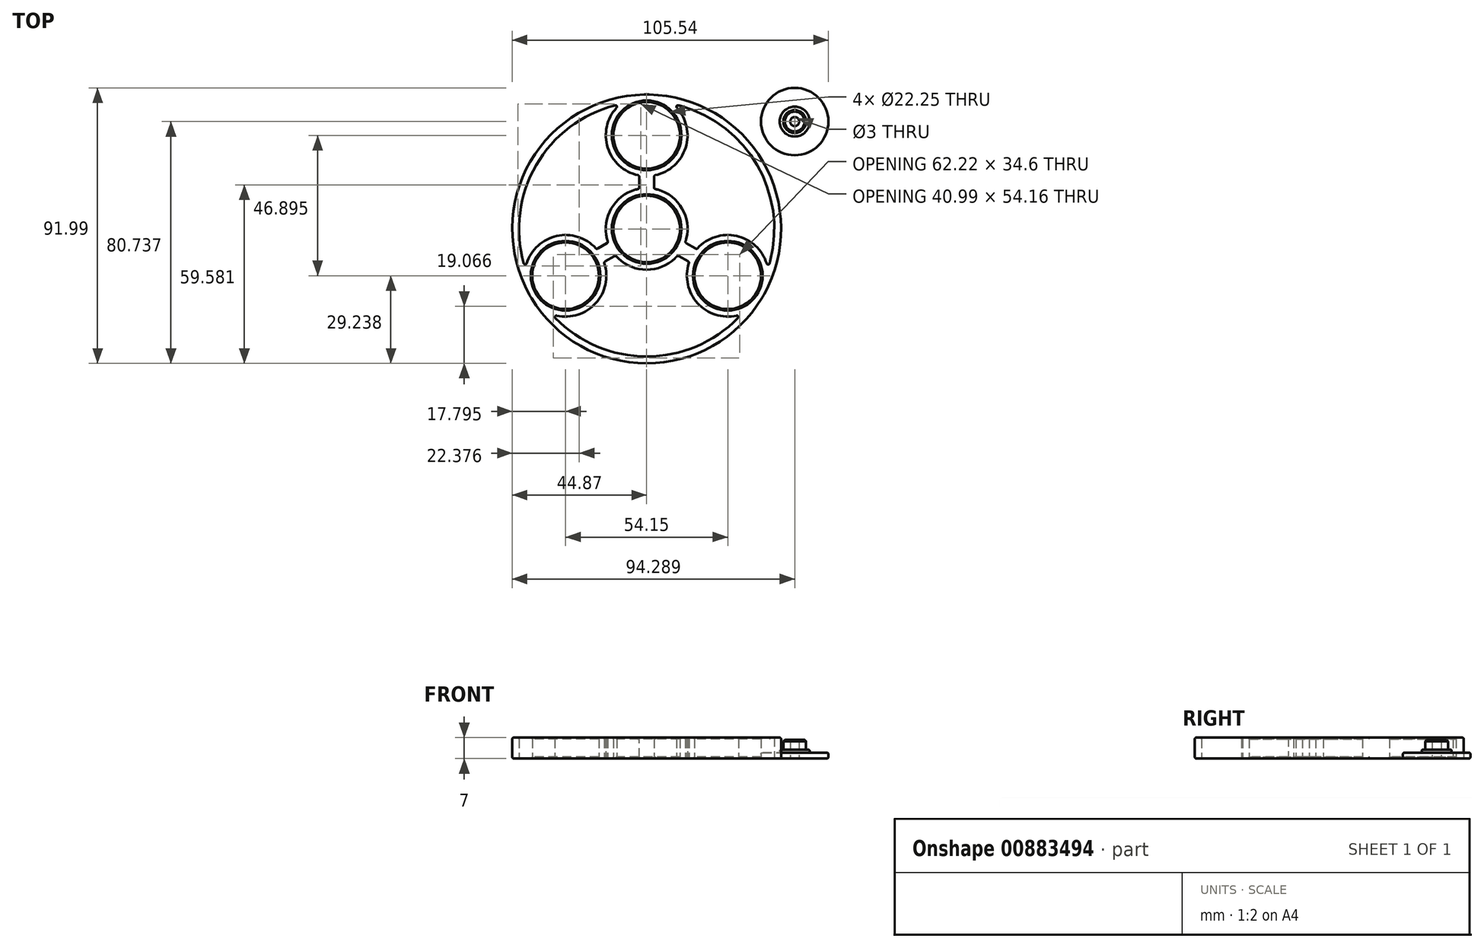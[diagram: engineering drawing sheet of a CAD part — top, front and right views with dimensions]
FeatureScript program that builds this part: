
annotation { "Feature Type Name" : "Feature", "Feature Type Description" : "" }
export const myFeature = defineFeature(function(context is Context, id is Id, definition is map)
    precondition{}
    {
        {
            var Q0;
            Q0=qCreatedBy(makeId("Top.planeOp"),FACE);
            var sketch = newSketch(context, id + "F0", { "sketchPlane" : qUnion([Q0])});
            skCircle(sketch, "E0", {"center": v(0, 0) * mm, "radius": 11.12 * mm});
            skArc(sketch, "E1", {"start": v(-2.5, 13.4) * mm, "mid": v(-11.8, 6.81) * mm, "end": v(-12.85, -4.53) * mm});
            skCircle(sketch, "E2", {"center": v(0, 31.26) * mm, "radius": 11.12 * mm});
            skArc(sketch, "E3", {"start": v(2.5, 17.87) * mm, "mid": v(13.18, 27.8) * mm, "end": v(8.76, 41.7) * mm});
            skLineSegment(sketch, "E4", {"start": v(-2.5, 17.87) * mm, "end": v(-2.5, 13.4) * mm});
            skLineSegment(sketch, "E5", {"start": v(2.5, 17.87) * mm, "end": v(2.5, 13.4) * mm});
            skArc(sketch, "E6.1.0", {"start": v(-16.73, -6.77) * mm, "mid": v(-30.66, -2.49) * mm, "end": v(-40.5, -13.26) * mm});
            skCircle(sketch, "E6.1.1", {"center": v(-27.07, -15.63) * mm, "radius": 11.12 * mm});
            skArc(sketch, "E6.1.2", {"start": v(-10.35, -8.86) * mm, "mid": v(0, -13.63) * mm, "end": v(10.35, -8.86) * mm});
            skLineSegment(sketch, "E6.1.4", {"start": v(-14.23, -11.1) * mm, "end": v(-10.35, -8.86) * mm});
            skLineSegment(sketch, "E6.1.5", {"start": v(-16.73, -6.77) * mm, "end": v(-12.85, -4.53) * mm});
            skArc(sketch, "E6.2.0", {"start": v(14.23, -11.1) * mm, "mid": v(17.49, -25.31) * mm, "end": v(31.73, -28.44) * mm});
            skCircle(sketch, "E6.2.1", {"center": v(27.07, -15.63) * mm, "radius": 11.12 * mm});
            skArc(sketch, "E6.2.2", {"start": v(12.85, -4.53) * mm, "mid": v(11.8, 6.81) * mm, "end": v(2.5, 13.4) * mm});
            skLineSegment(sketch, "E6.2.4", {"start": v(16.73, -6.77) * mm, "end": v(12.85, -4.53) * mm});
            skLineSegment(sketch, "E6.2.5", {"start": v(14.23, -11.1) * mm, "end": v(10.35, -8.86) * mm});
            skArc(sketch, "E7.trimOffspring", {"start": v(-10.35, -8.86) * mm, "mid": v(0, -13.62) * mm, "end": v(10.35, -8.86) * mm});
            skCircle(sketch, "E8", {"center": v(0, 0) * mm, "radius": 44.87 * mm});
            skArc(sketch, "E9", {"start": v(-31.73, -28.44) * mm, "mid": v(0, -42.6) * mm, "end": v(31.73, -28.44) * mm});
            skArc(sketch, "E10.trimOffspring", {"start": v(-39.26, -21.72) * mm, "mid": v(-38.87, -22.44) * mm, "end": v(-38.44, -23.14) * mm});
            skArc(sketch, "E11.trimOffspring", {"start": v(-31.73, -28.44) * mm, "mid": v(-17.49, -25.31) * mm, "end": v(-14.23, -11.1) * mm});
            skArc(sketch, "E12.trimOffspring", {"start": v(-8.76, 41.7) * mm, "mid": v(-36.9, 21.3) * mm, "end": v(-40.5, -13.26) * mm});
            skArc(sketch, "E13.trimOffspring", {"start": v(-8.76, 41.7) * mm, "mid": v(-13.18, 27.8) * mm, "end": v(-2.5, 17.87) * mm});
            skArc(sketch, "E14.trimOffspring", {"start": v(0.82, 44.86) * mm, "mid": v(0, 44.89) * mm, "end": v(-0.82, 44.86) * mm});
            skArc(sketch, "E15.trimOffspring", {"start": v(40.5, -13.26) * mm, "mid": v(30.66, -2.49) * mm, "end": v(16.73, -6.77) * mm});
            skArc(sketch, "E16.trimOffspring", {"start": v(40.5, -13.26) * mm, "mid": v(36.9, 21.3) * mm, "end": v(8.76, 41.7) * mm});
            skArc(sketch, "E17.trimOffspring", {"start": v(38.44, -23.14) * mm, "mid": v(38.87, -22.44) * mm, "end": v(39.26, -21.72) * mm});
            skSolve(sketch);
        }
        {
            var Q0;
            Q0 = qSketchRegion(id + "F0", true);
            extrude(context, id + "F1", {"entities" : qUnion([Q0]), "depth" : 7 * mm, "offsetDistance" : 25 * mm});
        }
        {
            var Q0;
            Q0=makeQuery(id+"F1.opExtrude","CAP_EDGE",EDGE,{"disambiguationData":[OSD([sQuery(id+"F0.wireOp",EDGE,"E6.2.0")])],"isStart":false});
            var Q1;
            Q1=makeQuery(id+"F1.opExtrude","CAP_EDGE",EDGE,{"disambiguationData":[OSD([sQuery(id+"F0.wireOp",EDGE,"E6.2.2")])],"isStart":false});
            var Q2;
            {var subQ0=sQuery(id+"F0.wireOp",EDGE,"E8");Q2=makeQuery(id+"F1.opExtrude","CAP_EDGE",EDGE,{"disambiguationData":[OSD([subQ0]),TDD([makeQuery(id+"F0.imprint","IMPRINT",EDGE,{"disambiguationData":[TD([[makeQuery(id+"F0.imprint","INTERSECT",VERTEX,{"disambiguationData":[OD(0.0)],"derivedFrom":[subQ0,sQuery(id+"F0.wireOp",EDGE,"E14.trimOffspring")]}),1.0]])],"derivedFrom":subQ0})])],"isStart":false});}
            var Q3;
            {var subQ0=sQuery(id+"F0.wireOp",EDGE,"E8");Q3=makeQuery(id+"F1.opExtrude","CAP_EDGE",EDGE,{"disambiguationData":[OSD([subQ0]),TDD([makeQuery(id+"F0.imprint","IMPRINT",EDGE,{"disambiguationData":[TD([[makeQuery(id+"F0.imprint","INTERSECT",VERTEX,{"disambiguationData":[OD(1.0)],"derivedFrom":[subQ0,sQuery(id+"F0.wireOp",EDGE,"E10.trimOffspring")]}),-1.0]])],"derivedFrom":subQ0})])],"isStart":false});}
            var Q4;
            Q4=makeQuery(id+"F1.opExtrude","CAP_EDGE",EDGE,{"disambiguationData":[OSD([sQuery(id+"F0.wireOp",EDGE,"E7.trimOffspring")])],"isStart":false});
            var Q5;
            Q5=makeQuery(id+"F1.opExtrude","CAP_EDGE",EDGE,{"disambiguationData":[OSD([sQuery(id+"F0.wireOp",EDGE,"E1")])],"isStart":false});
            var Q6;
            Q6=makeQuery(id+"F1.opExtrude","CAP_EDGE",EDGE,{"disambiguationData":[OSD([sQuery(id+"F0.wireOp",EDGE,"E9")])],"isStart":false});
            var Q7;
            Q7=makeQuery(id+"F1.opExtrude","CAP_EDGE",EDGE,{"disambiguationData":[OSD([sQuery(id+"F0.wireOp",EDGE,"E4")])],"isStart":false});
            var Q8;
            Q8=makeQuery(id+"F1.opExtrude","CAP_EDGE",EDGE,{"disambiguationData":[OSD([sQuery(id+"F0.wireOp",EDGE,"E15.trimOffspring")])],"isStart":false});
            var Q9;
            Q9=makeQuery(id+"F1.opExtrude","CAP_EDGE",EDGE,{"disambiguationData":[OSD([sQuery(id+"F0.wireOp",EDGE,"E5")])],"isStart":false});
            var Q10;
            Q10=makeQuery(id+"F1.opExtrude","CAP_EDGE",EDGE,{"disambiguationData":[OSD([sQuery(id+"F0.wireOp",EDGE,"E13.trimOffspring")])],"isStart":false});
            var Q11;
            Q11=makeQuery(id+"F1.opExtrude","CAP_EDGE",EDGE,{"disambiguationData":[OSD([sQuery(id+"F0.wireOp",EDGE,"E6.1.0")])],"isStart":false});
            var Q12;
            {var subQ0=sQuery(id+"F0.wireOp",EDGE,"E8");Q12=makeQuery(id+"F1.opExtrude","CAP_EDGE",EDGE,{"disambiguationData":[OSD([subQ0]),TDD([makeQuery(id+"F0.imprint","IMPRINT",EDGE,{"disambiguationData":[TD([[makeQuery(id+"F0.imprint","INTERSECT",VERTEX,{"disambiguationData":[OD(0.0)],"derivedFrom":[subQ0,sQuery(id+"F0.wireOp",EDGE,"E10.trimOffspring")]}),1.0]])],"derivedFrom":subQ0})])],"isStart":false});}
            var Q13;
            Q13=makeQuery(id+"F1.opExtrude","CAP_EDGE",EDGE,{"disambiguationData":[OSD([sQuery(id+"F0.wireOp",EDGE,"E11.trimOffspring")])],"isStart":false});
            var Q14;
            Q14=makeQuery(id+"F1.opExtrude","CAP_EDGE",EDGE,{"disambiguationData":[OSD([sQuery(id+"F0.wireOp",EDGE,"E3")])],"isStart":false});
            var Q15;
            Q15=makeQuery(id+"F1.opExtrude","CAP_EDGE",EDGE,{"disambiguationData":[OSD([sQuery(id+"F0.wireOp",EDGE,"E12.trimOffspring")])],"isStart":false});
            var Q16;
            Q16=makeQuery(id+"F1.opExtrude","CAP_EDGE",EDGE,{"disambiguationData":[OSD([sQuery(id+"F0.wireOp",EDGE,"E6.1.0")])],"isStart":true});
            var Q17;
            Q17=makeQuery(id+"F1.opExtrude","SWEPT_EDGE",EDGE,{"disambiguationData":[OSD([sQuery(id+"F0.wireOp",EDGE,"E4"),sQuery(id+"F0.wireOp",EDGE,"E1")])]});
            var Q18;
            Q18=makeQuery(id+"F1.opExtrude","CAP_EDGE",EDGE,{"disambiguationData":[OSD([sQuery(id+"F0.wireOp",EDGE,"E11.trimOffspring")])],"isStart":true});
            var Q19;
            Q19=makeQuery(id+"F1.opExtrude","SWEPT_EDGE",EDGE,{"disambiguationData":[OSD([sQuery(id+"F0.wireOp",EDGE,"E6.1.4"),sQuery(id+"F0.wireOp",EDGE,"E7.trimOffspring")])]});
            var Q20;
            Q20=makeQuery(id+"F1.opExtrude","CAP_EDGE",EDGE,{"disambiguationData":[OSD([sQuery(id+"F0.wireOp",EDGE,"E6.2.4")])],"isStart":false});
            var Q21;
            Q21=makeQuery(id+"F1.opExtrude","SWEPT_EDGE",EDGE,{"disambiguationData":[OSD([sQuery(id+"F0.wireOp",EDGE,"E6.1.0"),sQuery(id+"F0.wireOp",EDGE,"E6.1.5")])]});
            var Q22;
            {var subQ0=sQuery(id+"F0.wireOp",EDGE,"E8");Q22=makeQuery(id+"F1.opExtrude","CAP_EDGE",EDGE,{"disambiguationData":[OSD([subQ0]),TDD([makeQuery(id+"F0.imprint","IMPRINT",EDGE,{"disambiguationData":[TD([[makeQuery(id+"F0.imprint","INTERSECT",VERTEX,{"disambiguationData":[OD(0.0)],"derivedFrom":[subQ0,sQuery(id+"F0.wireOp",EDGE,"E10.trimOffspring")]}),1.0]])],"derivedFrom":subQ0})])],"isStart":true});}
            var Q23;
            Q23=makeQuery(id+"F1.opExtrude","CAP_EDGE",EDGE,{"disambiguationData":[OSD([sQuery(id+"F0.wireOp",EDGE,"E15.trimOffspring")])],"isStart":true});
            var Q24;
            Q24=makeQuery(id+"F1.opExtrude","SWEPT_EDGE",EDGE,{"disambiguationData":[OSD([sQuery(id+"F0.wireOp",EDGE,"E3"),sQuery(id+"F0.wireOp",EDGE,"E5")])]});
            var Q25;
            Q25=makeQuery(id+"F1.opExtrude","SWEPT_EDGE",EDGE,{"disambiguationData":[OSD([sQuery(id+"F0.wireOp",EDGE,"E6.1.0"),sQuery(id+"F0.wireOp",EDGE,"E12.trimOffspring")])]});
            var Q26;
            Q26=makeQuery(id+"F1.opExtrude","CAP_EDGE",EDGE,{"disambiguationData":[OSD([sQuery(id+"F0.wireOp",EDGE,"E14.trimOffspring")])],"isStart":false});
            var Q27;
            Q27=makeQuery(id+"F1.opExtrude","SWEPT_EDGE",EDGE,{"disambiguationData":[OSD([sQuery(id+"F0.wireOp",EDGE,"E6.2.4"),sQuery(id+"F0.wireOp",EDGE,"E6.2.2")])]});
            var Q28;
            Q28=makeQuery(id+"F1.opExtrude","CAP_EDGE",EDGE,{"disambiguationData":[OSD([sQuery(id+"F0.wireOp",EDGE,"E9")])],"isStart":true});
            var Q29;
            Q29=makeQuery(id+"F1.opExtrude","CAP_EDGE",EDGE,{"disambiguationData":[OSD([sQuery(id+"F0.wireOp",EDGE,"E6.1.4")])],"isStart":false});
            var Q30;
            Q30=makeQuery(id+"F1.opExtrude","CAP_EDGE",EDGE,{"disambiguationData":[OSD([sQuery(id+"F0.wireOp",EDGE,"E3")])],"isStart":true});
            var Q31;
            Q31=makeQuery(id+"F1.opExtrude","SWEPT_EDGE",EDGE,{"disambiguationData":[OSD([sQuery(id+"F0.wireOp",EDGE,"E5"),sQuery(id+"F0.wireOp",EDGE,"E6.2.2")])]});
            var Q32;
            {var subQ0=sQuery(id+"F0.wireOp",EDGE,"E8");Q32=makeQuery(id+"F1.opExtrude","CAP_EDGE",EDGE,{"disambiguationData":[OSD([subQ0]),TDD([makeQuery(id+"F0.imprint","IMPRINT",EDGE,{"disambiguationData":[TD([[makeQuery(id+"F0.imprint","INTERSECT",VERTEX,{"disambiguationData":[OD(0.0)],"derivedFrom":[subQ0,sQuery(id+"F0.wireOp",EDGE,"E14.trimOffspring")]}),1.0]])],"derivedFrom":subQ0})])],"isStart":true});}
            var Q33;
            Q33=makeQuery(id+"F1.opExtrude","CAP_EDGE",EDGE,{"disambiguationData":[OSD([sQuery(id+"F0.wireOp",EDGE,"E6.2.5")])],"isStart":false});
            var Q34;
            Q34=makeQuery(id+"F1.opExtrude","CAP_EDGE",EDGE,{"disambiguationData":[OSD([sQuery(id+"F0.wireOp",EDGE,"E10.trimOffspring")])],"isStart":false});
            var Q35;
            Q35=makeQuery(id+"F1.opExtrude","CAP_EDGE",EDGE,{"disambiguationData":[OSD([sQuery(id+"F0.wireOp",EDGE,"E17.trimOffspring")])],"isStart":false});
            var Q36;
            Q36=makeQuery(id+"F1.opExtrude","CAP_EDGE",EDGE,{"disambiguationData":[OSD([sQuery(id+"F0.wireOp",EDGE,"E7.trimOffspring")])],"isStart":true});
            var Q37;
            Q37=makeQuery(id+"F1.opExtrude","CAP_EDGE",EDGE,{"disambiguationData":[OSD([sQuery(id+"F0.wireOp",EDGE,"E6.2.2")])],"isStart":true});
            var Q38;
            Q38=makeQuery(id+"F1.opExtrude","CAP_EDGE",EDGE,{"disambiguationData":[OSD([sQuery(id+"F0.wireOp",EDGE,"E12.trimOffspring")])],"isStart":true});
            var Q39;
            Q39=makeQuery(id+"F1.opExtrude","SWEPT_EDGE",EDGE,{"disambiguationData":[OSD([sQuery(id+"F0.wireOp",EDGE,"E6.2.4"),sQuery(id+"F0.wireOp",EDGE,"E15.trimOffspring")])]});
            var Q40;
            Q40=makeQuery(id+"F1.opExtrude","CAP_EDGE",EDGE,{"disambiguationData":[OSD([sQuery(id+"F0.wireOp",EDGE,"E13.trimOffspring")])],"isStart":true});
            var Q41;
            Q41=makeQuery(id+"F1.opExtrude","SWEPT_EDGE",EDGE,{"disambiguationData":[OSD([sQuery(id+"F0.wireOp",EDGE,"E15.trimOffspring"),sQuery(id+"F0.wireOp",EDGE,"E16.trimOffspring")])]});
            var Q42;
            Q42=makeQuery(id+"F1.opExtrude","SWEPT_EDGE",EDGE,{"disambiguationData":[OSD([sQuery(id+"F0.wireOp",EDGE,"E9"),sQuery(id+"F0.wireOp",EDGE,"E11.trimOffspring")])]});
            var Q43;
            {var subQ0=sQuery(id+"F0.wireOp",EDGE,"E8");Q43=makeQuery(id+"F1.opExtrude","CAP_EDGE",EDGE,{"disambiguationData":[OSD([subQ0]),TDD([makeQuery(id+"F0.imprint","IMPRINT",EDGE,{"disambiguationData":[TD([[makeQuery(id+"F0.imprint","INTERSECT",VERTEX,{"disambiguationData":[OD(1.0)],"derivedFrom":[subQ0,sQuery(id+"F0.wireOp",EDGE,"E10.trimOffspring")]}),-1.0]])],"derivedFrom":subQ0})])],"isStart":true});}
            var Q44;
            Q44=makeQuery(id+"F1.opExtrude","SWEPT_EDGE",EDGE,{"disambiguationData":[OSD([sQuery(id+"F0.wireOp",EDGE,"E6.1.5"),sQuery(id+"F0.wireOp",EDGE,"E1")])]});
            var Q45;
            Q45=makeQuery(id+"F1.opExtrude","CAP_EDGE",EDGE,{"disambiguationData":[OSD([sQuery(id+"F0.wireOp",EDGE,"E16.trimOffspring")])],"isStart":true});
            var Q46;
            Q46=makeQuery(id+"F1.opExtrude","CAP_EDGE",EDGE,{"disambiguationData":[OSD([sQuery(id+"F0.wireOp",EDGE,"E6.2.0")])],"isStart":true});
            var Q47;
            Q47=makeQuery(id+"F1.opExtrude","SWEPT_EDGE",EDGE,{"disambiguationData":[OSD([sQuery(id+"F0.wireOp",EDGE,"E6.2.0"),sQuery(id+"F0.wireOp",EDGE,"E9")])]});
            var Q48;
            Q48=makeQuery(id+"F1.opExtrude","SWEPT_EDGE",EDGE,{"disambiguationData":[OSD([sQuery(id+"F0.wireOp",EDGE,"E4"),sQuery(id+"F0.wireOp",EDGE,"E13.trimOffspring")])]});
            var Q49;
            Q49=makeQuery(id+"F1.opExtrude","CAP_EDGE",EDGE,{"disambiguationData":[OSD([sQuery(id+"F0.wireOp",EDGE,"E1")])],"isStart":true});
            var Q50;
            Q50=makeQuery(id+"F1.opExtrude","SWEPT_EDGE",EDGE,{"disambiguationData":[OSD([sQuery(id+"F0.wireOp",EDGE,"E12.trimOffspring"),sQuery(id+"F0.wireOp",EDGE,"E13.trimOffspring")])]});
            var Q51;
            Q51=makeQuery(id+"F1.opExtrude","CAP_EDGE",EDGE,{"disambiguationData":[OSD([sQuery(id+"F0.wireOp",EDGE,"E6.1.5")])],"isStart":false});
            var Q52;
            Q52=makeQuery(id+"F1.opExtrude","SWEPT_EDGE",EDGE,{"disambiguationData":[OSD([sQuery(id+"F0.wireOp",EDGE,"E6.2.5"),sQuery(id+"F0.wireOp",EDGE,"E7.trimOffspring")])]});
            var Q53;
            Q53=makeQuery(id+"F1.opExtrude","CAP_EDGE",EDGE,{"disambiguationData":[OSD([sQuery(id+"F0.wireOp",EDGE,"E5")])],"isStart":true});
            var Q54;
            Q54=makeQuery(id+"F1.opExtrude","SWEPT_EDGE",EDGE,{"disambiguationData":[OSD([sQuery(id+"F0.wireOp",EDGE,"E3"),sQuery(id+"F0.wireOp",EDGE,"E16.trimOffspring")])]});
            var Q55;
            Q55=makeQuery(id+"F1.opExtrude","CAP_EDGE",EDGE,{"disambiguationData":[OSD([sQuery(id+"F0.wireOp",EDGE,"E6.2.4")])],"isStart":true});
            var Q56;
            Q56=makeQuery(id+"F1.opExtrude","CAP_EDGE",EDGE,{"disambiguationData":[OSD([sQuery(id+"F0.wireOp",EDGE,"E6.1.5")])],"isStart":true});
            var Q57;
            Q57=makeQuery(id+"F1.opExtrude","SWEPT_EDGE",EDGE,{"disambiguationData":[OSD([sQuery(id+"F0.wireOp",EDGE,"E6.1.4"),sQuery(id+"F0.wireOp",EDGE,"E11.trimOffspring")])]});
            var Q58;
            Q58=makeQuery(id+"F1.opExtrude","CAP_EDGE",EDGE,{"disambiguationData":[OSD([sQuery(id+"F0.wireOp",EDGE,"E17.trimOffspring")])],"isStart":true});
            var Q59;
            Q59=makeQuery(id+"F1.opExtrude","CAP_EDGE",EDGE,{"disambiguationData":[OSD([sQuery(id+"F0.wireOp",EDGE,"E6.2.5")])],"isStart":true});
            var Q60;
            Q60=makeQuery(id+"F1.opExtrude","CAP_EDGE",EDGE,{"disambiguationData":[OSD([sQuery(id+"F0.wireOp",EDGE,"E10.trimOffspring")])],"isStart":true});
            var Q61;
            Q61=makeQuery(id+"F1.opExtrude","CAP_EDGE",EDGE,{"disambiguationData":[OSD([sQuery(id+"F0.wireOp",EDGE,"E6.1.4")])],"isStart":true});
            var Q62;
            {var subQ0=sQuery(id+"F0.wireOp",EDGE,"E10.trimOffspring");var subQ1=sQuery(id+"F0.wireOp",EDGE,"E8");Q62=makeQuery(id+"F1.opExtrude","SWEPT_EDGE",EDGE,{"disambiguationData":[OSD([subQ1,subQ0]),TDD([makeQuery(id+"F0.imprint","INTERSECT",VERTEX,{"disambiguationData":[OD(0.0)],"derivedFrom":[subQ1,subQ0]})])]});}
            var Q63;
            Q63=makeQuery(id+"F1.opExtrude","CAP_EDGE",EDGE,{"disambiguationData":[OSD([sQuery(id+"F0.wireOp",EDGE,"E4")])],"isStart":true});
            var Q64;
            Q64=makeQuery(id+"F1.opExtrude","SWEPT_EDGE",EDGE,{"disambiguationData":[OSD([sQuery(id+"F0.wireOp",EDGE,"E6.2.0"),sQuery(id+"F0.wireOp",EDGE,"E6.2.5")])]});
            var Q65;
            {var subQ0=sQuery(id+"F0.wireOp",EDGE,"E10.trimOffspring");var subQ1=sQuery(id+"F0.wireOp",EDGE,"E8");Q65=makeQuery(id+"F1.opExtrude","SWEPT_EDGE",EDGE,{"disambiguationData":[OSD([subQ1,subQ0]),TDD([makeQuery(id+"F0.imprint","INTERSECT",VERTEX,{"disambiguationData":[OD(1.0)],"derivedFrom":[subQ1,subQ0]})])]});}
            var Q66;
            Q66=makeQuery(id+"F1.opExtrude","CAP_EDGE",EDGE,{"disambiguationData":[OSD([sQuery(id+"F0.wireOp",EDGE,"E14.trimOffspring")])],"isStart":true});
            var Q67;
            {var subQ0=sQuery(id+"F0.wireOp",EDGE,"E8");Q67=makeQuery(id+"F1.opExtrude","SWEPT_FACE",FACE,{"disambiguationData":[OSD([subQ0]),TDD([makeQuery(id+"F0.imprint","IMPRINT",EDGE,{"disambiguationData":[TD([[makeQuery(id+"F0.imprint","INTERSECT",VERTEX,{"disambiguationData":[OD(0.0)],"derivedFrom":[subQ0,sQuery(id+"F0.wireOp",EDGE,"E14.trimOffspring")]}),1.0]])],"derivedFrom":subQ0})])]});}
            var Q68;
            {var subQ0=sQuery(id+"F0.wireOp",EDGE,"E17.trimOffspring");var subQ1=sQuery(id+"F0.wireOp",EDGE,"E8");Q68=makeQuery(id+"F1.opExtrude","SWEPT_EDGE",EDGE,{"disambiguationData":[OSD([subQ1,subQ0]),TDD([makeQuery(id+"F0.imprint","INTERSECT",VERTEX,{"disambiguationData":[OD(1.0)],"derivedFrom":[subQ1,subQ0]})])]});}
            var Q69;
            Q69=makeQuery(id+"F1.opExtrude","SWEPT_FACE",FACE,{"disambiguationData":[OSD([sQuery(id+"F0.wireOp",EDGE,"E17.trimOffspring")])]});
            var Q70;
            {var subQ0=sQuery(id+"F0.wireOp",EDGE,"E14.trimOffspring");var subQ1=sQuery(id+"F0.wireOp",EDGE,"E8");Q70=makeQuery(id+"F1.opExtrude","SWEPT_EDGE",EDGE,{"disambiguationData":[OSD([subQ1,subQ0]),TDD([makeQuery(id+"F0.imprint","INTERSECT",VERTEX,{"disambiguationData":[OD(1.0)],"derivedFrom":[subQ1,subQ0]})])]});}
            fillet(context, id + "F2", {"entities" : qUnion([Q0, Q1, Q2, Q3, Q4, Q5, Q6, Q7, Q8, Q9, Q10, Q11, Q12, Q13, Q14, Q15, Q16, Q17, Q18, Q19, Q20, Q21, Q22, Q23, Q24, Q25, Q26, Q27, Q28, Q29, Q30, Q31, Q32, Q33, Q34, Q35, Q36, Q37, Q38, Q39, Q40, Q41, Q42, Q43, Q44, Q45, Q46, Q47, Q48, Q49, Q50, Q51, Q52, Q53, Q54, Q55, Q56, Q57, Q58, Q59, Q60, Q61, Q62, Q63, Q64, Q65, Q66, Q67, Q68, Q69, Q70]), "radius" : 0.5 * mm, "tangentPropagation" : true, "allowEdgeOverflow" : false});
        }
        {
            var Q0;
            Q0=makeQuery(id+"F1.opExtrude","CAP_EDGE",EDGE,{"disambiguationData":[OSD([sQuery(id+"F0.wireOp",EDGE,"E6.2.1")])],"isStart":false});
            var Q1;
            Q1=makeQuery(id+"F1.opExtrude","CAP_EDGE",EDGE,{"disambiguationData":[OSD([sQuery(id+"F0.wireOp",EDGE,"E6.2.1")])],"isStart":true});
            var Q2;
            Q2=makeQuery(id+"F1.opExtrude","CAP_EDGE",EDGE,{"disambiguationData":[OSD([sQuery(id+"F0.wireOp",EDGE,"E0")])],"isStart":true});
            var Q3;
            Q3=makeQuery(id+"F1.opExtrude","CAP_EDGE",EDGE,{"disambiguationData":[OSD([sQuery(id+"F0.wireOp",EDGE,"E0")])],"isStart":false});
            var Q4;
            Q4=makeQuery(id+"F1.opExtrude","CAP_EDGE",EDGE,{"disambiguationData":[OSD([sQuery(id+"F0.wireOp",EDGE,"E2")])],"isStart":false});
            var Q5;
            Q5=makeQuery(id+"F1.opExtrude","CAP_EDGE",EDGE,{"disambiguationData":[OSD([sQuery(id+"F0.wireOp",EDGE,"E2")])],"isStart":true});
            var Q6;
            Q6=makeQuery(id+"F1.opExtrude","CAP_EDGE",EDGE,{"disambiguationData":[OSD([sQuery(id+"F0.wireOp",EDGE,"E6.1.1")])],"isStart":false});
            var Q7;
            Q7=makeQuery(id+"F1.opExtrude","CAP_EDGE",EDGE,{"disambiguationData":[OSD([sQuery(id+"F0.wireOp",EDGE,"E6.1.1")])],"isStart":true});
            chamfer(context, id + "F3", {"entities" : qUnion([Q0, Q1, Q2, Q3, Q4, Q5, Q6, Q7]), "width" : 0.5 * mm, "tangentPropagation" : true});
        }
        {
            var Q0;
            Q0=qCreatedBy(makeId("Top.planeOp"),FACE);
            var sketch = newSketch(context, id + "F4", { "sketchPlane" : qUnion([Q0])});
            skCircle(sketch, "E18", {"center": v(49.42, 35.87) * mm, "radius": 11.25 * mm});
            skCircle(sketch, "E19", {"center": v(49.42, 35.87) * mm, "radius": 5 * mm});
            skCircle(sketch, "E20", {"center": v(49.42, 35.87) * mm, "radius": 3.8 * mm});
            skCircle(sketch, "E21", {"center": v(49.42, 35.87) * mm, "radius": 1.5 * mm});
            skSolve(sketch);
        }
        {
            var Q0;
            Q0 = qSketchRegion(id + "F4", true);
            extrude(context, id + "F5", {"entities" : qUnion([Q0]), "depth" : 2 * mm, "offsetDistance" : 25 * mm});
        }
        {
            var Q0;
            Q0=makeQuery(id+"F4.imprint","IMPRINT",FACE,{"disambiguationData":[TD([[makeQuery(id+"F4.imprint","IMPRINT",EDGE,{"derivedFrom":sQuery(id+"F4.wireOp",EDGE,"E19")}),1.0]])]});
            extrude(context, id + "F6", {"entities" : qUnion([Q0]), "operationType" : NewBodyOperationType.ADD, "depth" : 3 * mm, "offsetDistance" : 25 * mm});
        }
        {
            var Q0;
            Q0=makeQuery(id+"F4.imprint","IMPRINT",FACE,{"disambiguationData":[TD([[makeQuery(id+"F4.imprint","IMPRINT",EDGE,{"derivedFrom":sQuery(id+"F4.wireOp",EDGE,"E20")}),1.0]])]});
            extrude(context, id + "F7", {"entities" : qUnion([Q0]), "operationType" : NewBodyOperationType.ADD, "depth" : 6.25 * mm, "offsetDistance" : 25 * mm});
        }
        {
            var Q0;
            Q0=makeQuery(id+"F7.opExtrude","CAP_EDGE",EDGE,{"disambiguationData":[OSD([sQuery(id+"F4.wireOp",EDGE,"E20")])],"isStart":false});
            chamfer(context, id + "F8", {"entities" : qUnion([Q0]), "width" : 0.5 * mm, "tangentPropagation" : true});
        }
        {
            var Q0;
            Q0=makeQuery(id+"F7.opExtrude","CAP_EDGE",EDGE,{"disambiguationData":[OSD([sQuery(id+"F4.wireOp",EDGE,"E21")])],"isStart":false});
            var Q1;
            Q1=makeQuery(id+"F6.opExtrude","CAP_EDGE",EDGE,{"disambiguationData":[OSD([sQuery(id+"F4.wireOp",EDGE,"E19")])],"isStart":false});
            var Q2;
            Q2=makeQuery(id+"F5.opExtrude","CAP_EDGE",EDGE,{"disambiguationData":[OSD([sQuery(id+"F4.wireOp",EDGE,"E19")])],"isStart":false});
            var Q3;
            Q3=makeQuery(id+"F5.opExtrude","CAP_EDGE",EDGE,{"disambiguationData":[OSD([sQuery(id+"F4.wireOp",EDGE,"E18")])],"isStart":false});
            var Q4;
            Q4=makeQuery(id+"F5.opExtrude","CAP_EDGE",EDGE,{"disambiguationData":[OSD([sQuery(id+"F4.wireOp",EDGE,"E18")])],"isStart":true});
            fillet(context, id + "F9", {"entities" : qUnion([Q0, Q1, Q2, Q3, Q4]), "radius" : 0.5 * mm, "tangentPropagation" : true, "allowEdgeOverflow" : false});
        }
        {
            var Q0;
            Q0=makeQuery(id+"F7.opExtrude","CAP_EDGE",EDGE,{"disambiguationData":[OSD([sQuery(id+"F4.wireOp",EDGE,"E21")])],"isStart":true});
            fillet(context, id + "F10", {"entities" : qUnion([Q0]), "radius" : 0.5 * mm, "tangentPropagation" : true, "allowEdgeOverflow" : false});
        }
    });
